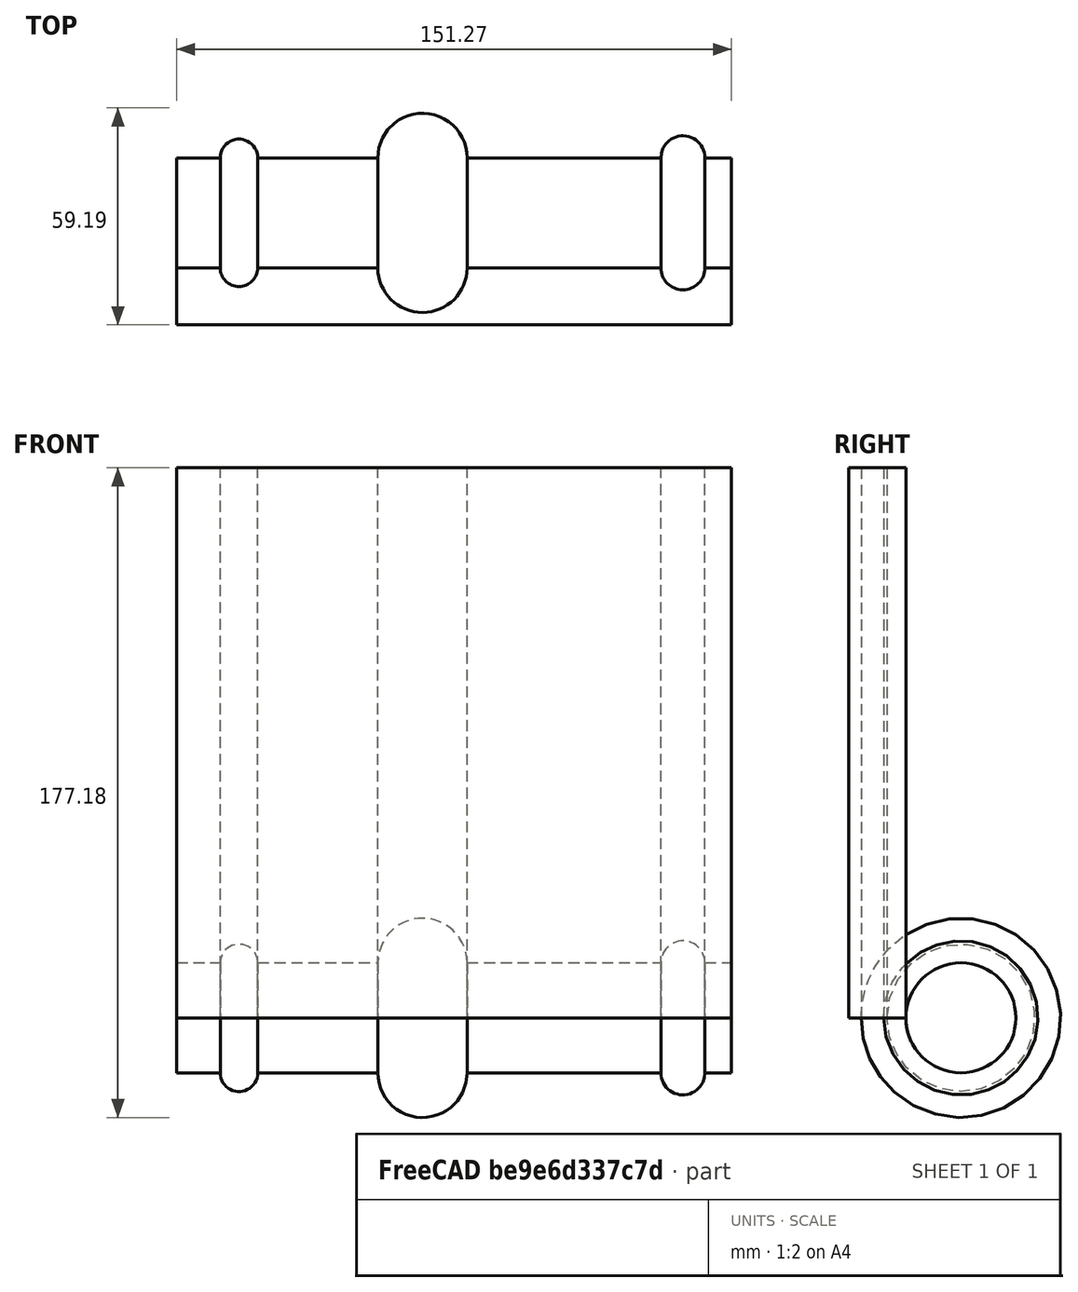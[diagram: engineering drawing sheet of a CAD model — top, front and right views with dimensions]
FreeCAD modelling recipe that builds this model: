
FCSTD DOCUMENT  (FreeCAD 0.20R29410 (Git))
Label: MangoJelly_Solutions_Tutorial_Ep8_3
License: All rights reserved
LicenseURL: http://en.wikipedia.org/wiki/All_rights_reserved
objects: Part::Feature×3, Sketcher::SketchObject×2, Part::Extrusion×1, PartDesign::SubShapeBinder×1, Part::Revolution×1, Part::Compound×1
note: 9 computed .brp shape members not serialized (recipe doc carries the construction recipe); baked Part::Feature solids carry a one-line shape summary decoded from their .brp

FEATURE [Sketcher::SketchObject] Sketch
  FullyConstrained = false
  sketch-geometry (10):
    g0: LineSegment StartX=-67.0527 StartY=0 StartZ=0 EndX=-55.1615 EndY=0 EndZ=0
    g1: LineSegment StartX=84.2203 StartY=0 StartZ=0 EndX=84.2203 EndY=-15.5793 EndZ=0
    g2: LineSegment StartX=84.2203 StartY=-15.5793 StartZ=0 EndX=-67.0527 EndY=-15.5793 EndZ=0
    g3: LineSegment StartX=-67.0527 StartY=-15.5793 StartZ=0 EndX=-67.0527 EndY=0 EndZ=0
    g4: ArcOfCircle CenterX=-50.0435 CenterY=0 CenterZ=0 NormalX=0 NormalY=0 NormalZ=1 AngleXU=0 Radius=5.118 StartAngle=3.14159 EndAngle=6.28319
    g5: ArcOfCircle CenterX=71.011 CenterY=0 CenterZ=0 NormalX=0 NormalY=0 NormalZ=1 AngleXU=0 Radius=6.015 StartAngle=3.14159 EndAngle=6.28319
    g6: ArcOfCircle CenterX=0 CenterY=0 CenterZ=0 NormalX=0 NormalY=0 NormalZ=1 AngleXU=0 Radius=12.1801 StartAngle=3.14159 EndAngle=6.28319
    g7: LineSegment StartX=-44.9255 StartY=-1.3e-15 StartZ=0 EndX=-12.1801 EndY=0 EndZ=0
    g8: LineSegment StartX=12.1801 StartY=0 StartZ=0 EndX=64.996 EndY=0 EndZ=0
    g9: LineSegment StartX=77.0261 StartY=0 StartZ=0 EndX=84.2203 EndY=0 EndZ=0
  constraints (22):
    c: Coincident(g9,g1)
    c: Coincident(g1,g2)
    c: Coincident(g2,g3)
    c: Coincident(g3,g0)
    c: Horizontal(g0)
    c: Horizontal(g2)
    c: Vertical(g1)
    c: Vertical(g3)
    c: PointOnObject(g0,g-1)
    c: PointOnObject(g4,g0)
    c: PointOnObject(g5,g0)
    c: Coincident(g6,g-1)
    c: PointOnObject(g6,g0)
    c: PointOnObject(g6,g0)
    c: PointOnObject(g5,g0)
    c: PointOnObject(g5,g0)
    c: Coincident(g0,g4)
    c: Coincident(g7,g4)
    c: PointOnObject(g7,g6)
    c: PointOnObject(g8,g6)
    c: PointOnObject(g8,g5)
    c: PointOnObject(g9,g5)
FEATURE [Part::Extrusion] Extrude
  Base = -> Sketch
  Dir = (0,0,1)
  DirMode = 2
  FaceMakerClass = Part::FaceMakerBullseye
  LengthFwd = 150
  LengthRev = 0
  Solid = true
  Symmetric = false
FEATURE [Sketcher::SketchObject] Sketch001
  FullyConstrained = false
  MapMode = 2
  Support = -> [Extrude]
  sketch-geometry (1):
    g0: LineSegment StartX=-67.7552 StartY=15 StartZ=0 EndX=84.393 EndY=15 EndZ=0
  constraints (2):
    c: Horizontal(g0)
    c: DistanceY(g-1,g0) = 15
FEATURE [PartDesign::SubShapeBinder] Binder
  BindCopyOnChange = 0
  BindMode = 0
  ClaimChildren = false
  Fuse = false
  MakeFace = true
  OffsetFill = false
  OffsetIntersection = false
  OffsetJoinType = 0
  OffsetOpenResult = false
  PartialLoad = false
  Relative = true
  Support = -> [Extrude[Edge21,Edge18,Edge15,Edge12,Edge9,Edge6,Edge3]]
  _Version = 2
FEATURE [Part::Revolution] Revolve
  Angle = 360
  Axis = (1,0,0)
  AxisLink = -> Sketch001 [Edge1]
  Base = (84.393,15,0)
  FaceMakerClass = Part::FaceMakerBullseye
  Solid = false
  Source = -> Binder
  Symmetric = false
FEATURE [Part::Feature] Face
  shape: bbox 2e-07 x 50.65 x 46.59 mm, 1 faces, 0 solids (baked)
FEATURE [Part::Feature] Face001
  shape: bbox 2e-07 x 50.65 x 46.59 mm, 1 faces, 0 solids (baked)
FEATURE [Part::Compound] Compound
  Links = -> [Revolve,Face,Face001]
FEATURE [Part::Feature] Compound_solid  label="Compound (Solid)"
  shape: bbox 151.3 x 60.85 x 54.36 mm, 9 faces (baked)
